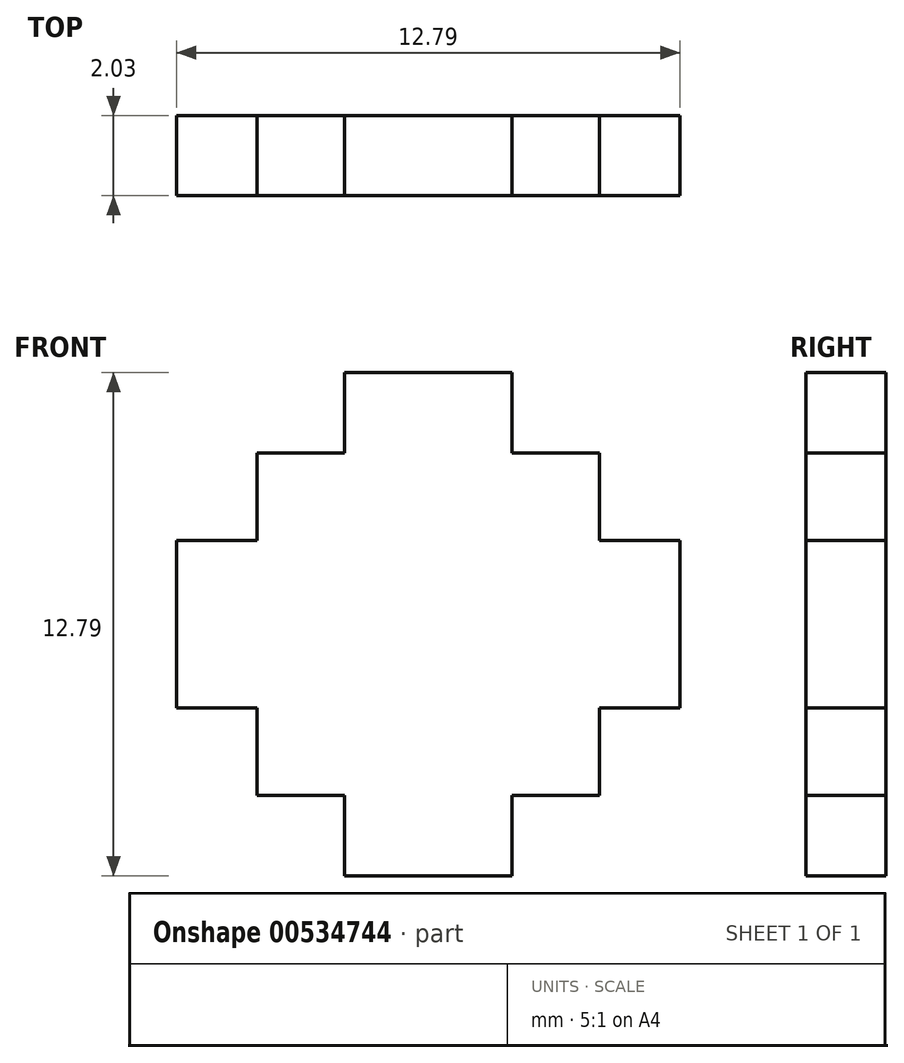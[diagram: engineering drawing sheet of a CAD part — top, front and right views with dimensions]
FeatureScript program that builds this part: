
annotation { "Feature Type Name" : "Feature", "Feature Type Description" : "" }
export const myFeature = defineFeature(function(context is Context, id is Id, definition is map)
    precondition{}
    {
        {
            var Q0;
            Q0=qCreatedBy(makeId("Front.planeOp"),FACE);
            var sketch = newSketch(context, id + "F0", { "sketchPlane" : qUnion([Q0])});
            skLineSegment(sketch, "E0", {"start": v(-17.35, 36.23) * mm, "end": v(-15.22, 36.23) * mm});
            skLineSegment(sketch, "E1", {"start": v(-15.22, 36.23) * mm, "end": v(-15.22, 34.18) * mm});
            skLineSegment(sketch, "E2", {"start": v(-15.22, 34.18) * mm, "end": v(-13, 34.18) * mm});
            skLineSegment(sketch, "E3", {"start": v(-13, 34.18) * mm, "end": v(-13, 31.96) * mm});
            skLineSegment(sketch, "E4", {"start": v(-13, 31.96) * mm, "end": v(-10.95, 31.96) * mm});
            skLineSegment(sketch, "E5", {"start": v(-10.95, 31.96) * mm, "end": v(-10.95, 29.83) * mm});
            skLineSegment(sketch, "E6", {"start": v(-17.35, 36.23) * mm, "end": v(-17.35, 28.94) * mm, "construction": true});
            skLineSegment(sketch, "E7.MirrorCS", {"start": v(-17.35, 36.23) * mm, "end": v(-19.48, 36.23) * mm});
            skLineSegment(sketch, "E8.MirrorCS", {"start": v(-19.48, 36.23) * mm, "end": v(-19.48, 34.18) * mm});
            skLineSegment(sketch, "E9.MirrorCS", {"start": v(-19.48, 34.18) * mm, "end": v(-21.7, 34.18) * mm});
            skLineSegment(sketch, "E10.MirrorCS", {"start": v(-21.7, 34.18) * mm, "end": v(-21.7, 31.96) * mm});
            skLineSegment(sketch, "E11.MirrorCS", {"start": v(-21.7, 31.96) * mm, "end": v(-23.74, 31.96) * mm});
            skLineSegment(sketch, "E12.MirrorCS", {"start": v(-23.74, 31.96) * mm, "end": v(-23.74, 29.83) * mm});
            skLineSegment(sketch, "E13", {"start": v(-23.74, 29.83) * mm, "end": v(-10.95, 29.83) * mm, "construction": true});
            skLineSegment(sketch, "E14.MirrorCS", {"start": v(-23.74, 27.7) * mm, "end": v(-23.74, 29.83) * mm});
            skLineSegment(sketch, "E15.MirrorCS", {"start": v(-21.7, 27.7) * mm, "end": v(-23.74, 27.7) * mm});
            skLineSegment(sketch, "E16.MirrorCS", {"start": v(-21.7, 25.48) * mm, "end": v(-21.7, 27.7) * mm});
            skLineSegment(sketch, "E17.MirrorCS", {"start": v(-19.48, 25.48) * mm, "end": v(-21.7, 25.48) * mm});
            skLineSegment(sketch, "E18.MirrorCS", {"start": v(-19.48, 23.44) * mm, "end": v(-19.48, 25.48) * mm});
            skLineSegment(sketch, "E19.MirrorCS", {"start": v(-17.35, 23.44) * mm, "end": v(-19.48, 23.44) * mm});
            skLineSegment(sketch, "E20.MirrorCS", {"start": v(-17.35, 23.44) * mm, "end": v(-15.22, 23.44) * mm});
            skLineSegment(sketch, "E21.MirrorCS", {"start": v(-15.22, 23.44) * mm, "end": v(-15.22, 25.48) * mm});
            skLineSegment(sketch, "E22.MirrorCS", {"start": v(-15.22, 25.48) * mm, "end": v(-13, 25.48) * mm});
            skLineSegment(sketch, "E23.MirrorCS", {"start": v(-13, 25.48) * mm, "end": v(-13, 27.7) * mm});
            skLineSegment(sketch, "E24.MirrorCS", {"start": v(-13, 27.7) * mm, "end": v(-10.95, 27.7) * mm});
            skLineSegment(sketch, "E25.MirrorCS", {"start": v(-10.95, 27.7) * mm, "end": v(-10.95, 29.83) * mm});
            skSolve(sketch);
        }
        {
            var Q0;
            Q0=makeQuery(id+"F0.imprint","IMPRINT",FACE,{"disambiguationData":[TD([[makeQuery(id+"F0.imprint","IMPRINT",EDGE,{"derivedFrom":sQuery(id+"F0.wireOp",EDGE,"E0")}),-1.0]])]});
            extrude(context, id + "F1", {"entities" : qUnion([Q0]), "depth" : 2.03 * mm, "offsetDistance" : 25.4 * mm});
        }
        {
            var Q0;
            Q0=qCreatedBy(makeId("Front.planeOp"),FACE);
            cPlane(context, id + "F2", {"entities" : qUnion([Q0]), "cplaneType" : CPlaneType.OFFSET, "offset" : 4.06 * mm, "width" : 152.4 * mm, "height" : 152.4 * mm});
        }
        {
            var Q0;
            Q0=qCreatedBy(id+"F2.planeOp",FACE);
            var sketch = newSketch(context, id + "F3", { "sketchPlane" : qUnion([Q0])});
            skText(sketch, "E26", { "text": "K", "fontName": "OpenSans-Regular.ttf"});
            const initialGuessF3  = {"E26": [-0.02028, 0.02669, 1, 0, 0.00618]};
            skSetInitialGuess(sketch, initialGuessF3);
            skSolve(sketch);
        }
        {
            var Q0;
            Q0 = qSketchRegion(id + "F3", true);
            extrude(context, id + "F4", {"entities" : qUnion([Q0]), "operationType" : NewBodyOperationType.REMOVE, "oppositeDirection" : true, "depth" : 0.5 * mm, "offsetDistance" : 25.4 * mm});
        }
    });
